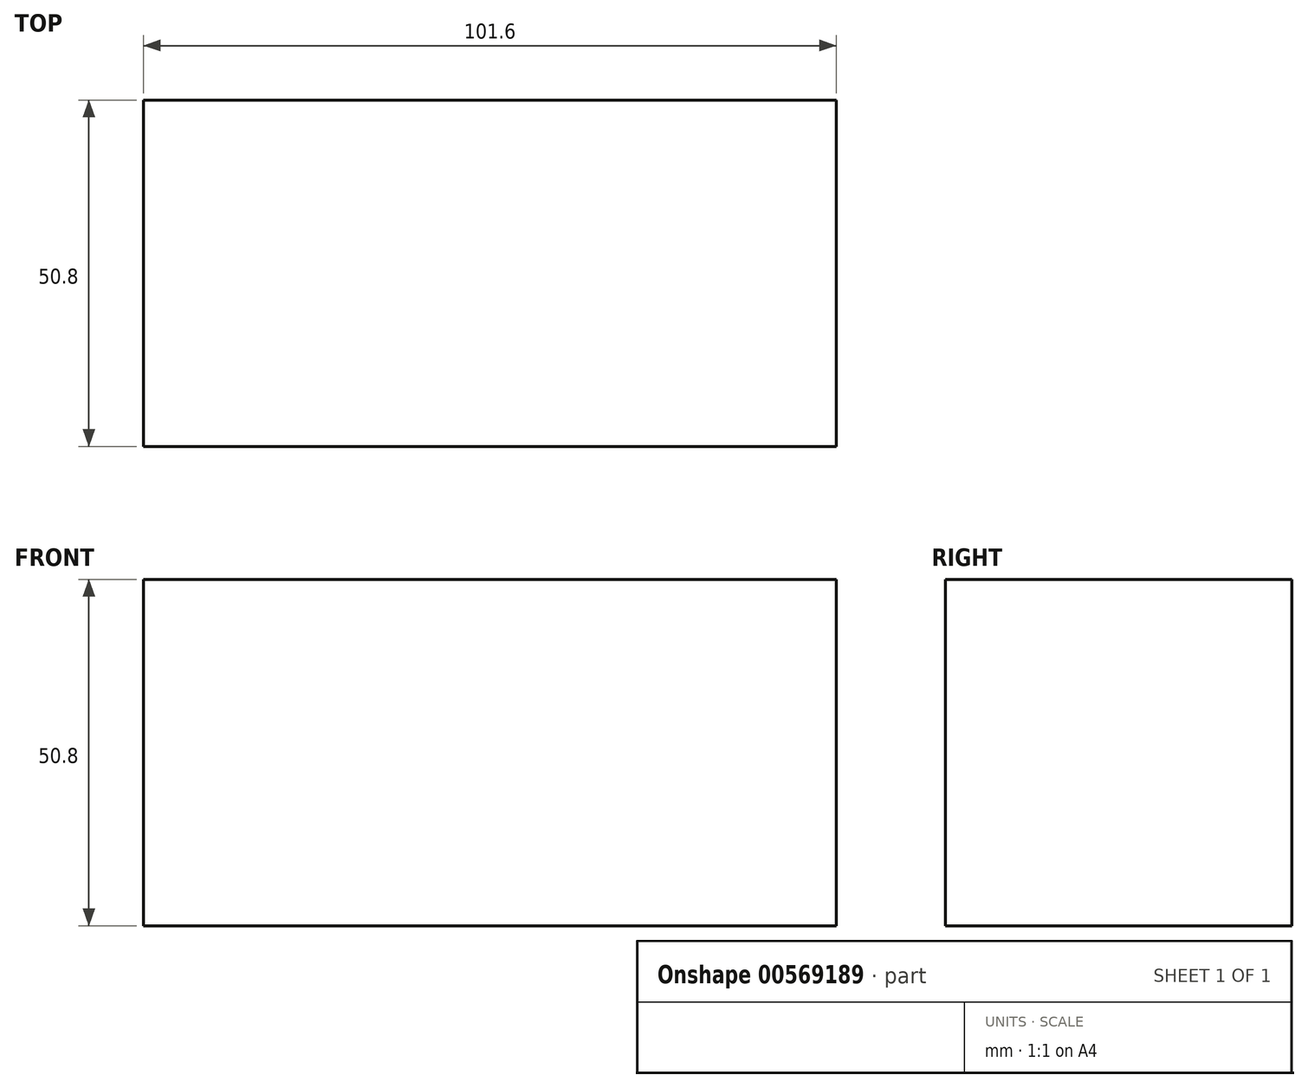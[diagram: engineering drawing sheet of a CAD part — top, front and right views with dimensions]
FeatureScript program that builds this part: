
annotation { "Feature Type Name" : "Feature", "Feature Type Description" : "" }
export const myFeature = defineFeature(function(context is Context, id is Id, definition is map)
    precondition{}
    {
        {
            var Q0;
            Q0=qCreatedBy(makeId("Front.planeOp"),FACE);
            var sketch = newSketch(context, id + "F0", { "sketchPlane" : qUnion([Q0])});
            skLineSegment(sketch, "E0.bottom", {"start": v(-25.4, 25.4) * mm, "end": v(76.2, 25.4) * mm});
            skLineSegment(sketch, "E0.top", {"start": v(-25.4, -25.4) * mm, "end": v(76.2, -25.4) * mm});
            skLineSegment(sketch, "E0.left", {"start": v(-25.4, 25.4) * mm, "end": v(-25.4, -25.4) * mm});
            skLineSegment(sketch, "E0.right", {"start": v(76.2, 25.4) * mm, "end": v(76.2, -25.4) * mm});
            skPoint(sketch, "E0.middle", {"position": v(25.4, 0) * mm});
            skSolve(sketch);
        }
        {
            var Q0;
            Q0=makeQuery(id+"F0.imprint","IMPRINT",FACE,{"disambiguationData":[TD([[makeQuery(id+"F0.imprint","IMPRINT",EDGE,{"derivedFrom":sQuery(id+"F0.wireOp",EDGE,"79NG03y4-AKBa-swYW-NuOs-akHqhjTvIVj8.bottom")}),1.0]])]});
            var Q1;
            Q1=makeQuery(id+"F0.imprint","IMPRINT",FACE,{"disambiguationData":[TD([[makeQuery(id+"F0.imprint","IMPRINT",EDGE,{"derivedFrom":sQuery(id+"F0.wireOp",EDGE,"E0.bottom")}),-1.0]])]});
            extrude(context, id + "F1", {"entities" : qUnion([Q0, Q1]), "endBound" : BoundingType.SYMMETRIC, "depth" : 50.8 * mm, "offsetDistance" : 25.4 * mm});
        }
    });
